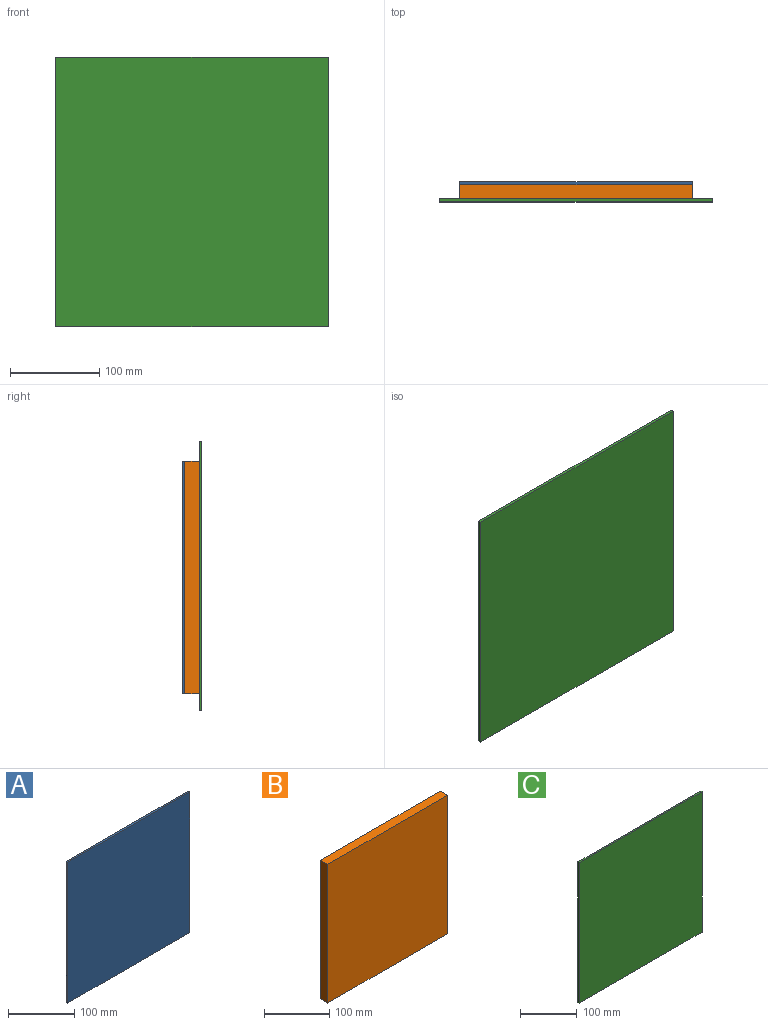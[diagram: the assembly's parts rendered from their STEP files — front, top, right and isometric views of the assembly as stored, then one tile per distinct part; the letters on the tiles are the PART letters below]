
ASSEMBLY  parts=3 mates=2
PART A: 6 faces, bbox 260.4x3.2x260.4 mm
  f0: plane 260.35x3.18mm, normal (1,0,0), area 826.6mm2, adj f1,f3,f4,f5
  f1: plane 260.35x3.18mm, normal (0,0,1), area 826.6mm2, adj f0,f2,f4,f5
  f2: plane 260.35x3.18mm, normal (-1,0,0), area 826.6mm2, adj f1,f3,f4,f5
  f3: plane 260.35x3.18mm, normal (0,0,-1), area 826.6mm2, adj f0,f2,f4,f5
  f4: plane 260.35x260.35mm, normal (0,-1,0), area 67782.1mm2, adj f0,f1,f2,f3
  f5: plane 260.35x260.35mm, normal (0,1,0), area 67782.1mm2, adj f0,f1,f2,f3
PART B: 6 faces, bbox 260.4x15.9x260.4 mm
  f0: plane 260.35x15.88mm, normal (1,0,0), area 4133.1mm2, adj f1,f3,f4,f5
  f1: plane 260.35x15.88mm, normal (0,0,1), area 4133.1mm2, adj f0,f2,f4,f5
  f2: plane 260.35x15.88mm, normal (-1,0,0), area 4133.1mm2, adj f1,f3,f4,f5
  f3: plane 260.35x15.88mm, normal (0,0,-1), area 4133.1mm2, adj f0,f2,f4,f5
  f4: plane 260.35x260.35mm, normal (0,-1,0), area 67782.1mm2, adj f0,f1,f2,f3
  f5: plane 260.35x260.35mm, normal (0,1,0), area 67782.1mm2, adj f0,f1,f2,f3
PART C: 6 faces, bbox 304.8x3.2x301.6 mm
  f0: plane 301.63x3.18mm, normal (1,0,0), area 957.7mm2, adj f1,f3,f4,f5
  f1: plane 304.8x3.18mm, normal (0,0,1), area 967.7mm2, adj f0,f2,f4,f5
  f2: plane 301.63x3.18mm, normal (-1,0,0), area 957.7mm2, adj f1,f3,f4,f5
  f3: plane 304.8x3.18mm, normal (0,0,-1), area 967.7mm2, adj f0,f2,f4,f5
  f4: plane 304.8x301.63mm, normal (0,-1,0), area 91935.3mm2, adj f0,f1,f2,f3
  f5: plane 304.8x301.63mm, normal (0,1,0), area 91935.3mm2, adj f0,f1,f2,f3
PLACE A at identity
PLACE B t=(0,-3.18,0)mm
PLACE C t=(0,-19.05,1.59)mm
MATE fastened C.f5 <-> B.f4  axis (0,1,0) through (0,-19.05,-445.28)mm
MATE fastened B.f5 <-> A.f4  axis (0,1,0) through (0,-3.18,-446.86)mm
